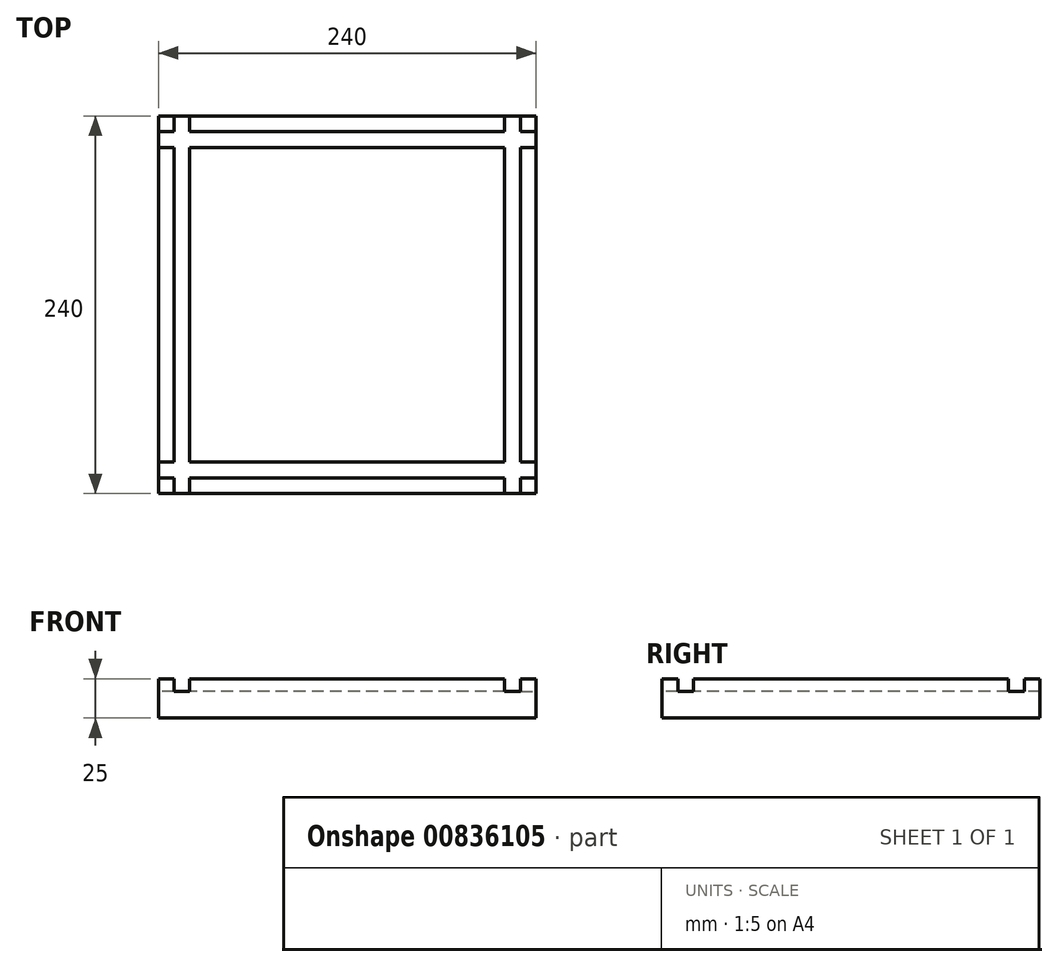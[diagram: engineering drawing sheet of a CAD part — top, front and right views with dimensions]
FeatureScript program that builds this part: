
annotation { "Feature Type Name" : "Feature", "Feature Type Description" : "" }
export const myFeature = defineFeature(function(context is Context, id is Id, definition is map)
    precondition{}
    {
        {
            var Q0;
            Q0=qCreatedBy(makeId("Top.planeOp"),FACE);
            var sketch = newSketch(context, id + "F0", { "sketchPlane" : qUnion([Q0])});
            skLineSegment(sketch, "E0.bottom", {"start": v(-120, 120) * mm, "end": v(120, 120) * mm});
            skLineSegment(sketch, "E0.top", {"start": v(-120, -120) * mm, "end": v(120, -120) * mm});
            skLineSegment(sketch, "E0.left", {"start": v(-120, 120) * mm, "end": v(-120, -120) * mm});
            skLineSegment(sketch, "E0.right", {"start": v(120, 120) * mm, "end": v(120, -120) * mm});
            skPoint(sketch, "E0.middle", {"position": v(0, 0) * mm});
            skSolve(sketch);
        }
        {
            var Q0;
            Q0 = qSketchRegion(id + "F0", true);
            extrude(context, id + "F1", {"entities" : qUnion([Q0]), "oppositeDirection" : true, "depth" : 25 * mm, "offsetDistance" : 25 * mm});
        }
        {
            var Q0;
            Q0=makeQuery(id+"F1.opExtrude","CAP_FACE",FACE,{"disambiguationData":[OSD([sQuery(id+"F0.wireOp",EDGE,"E0.bottom"),sQuery(id+"F0.wireOp",EDGE,"E0.top"),sQuery(id+"F0.wireOp",EDGE,"E0.left"),sQuery(id+"F0.wireOp",EDGE,"E0.right")])],"isStart":true});
            var sketch = newSketch(context, id + "F2", { "sketchPlane" : qUnion([Q0])});
            skLineSegment(sketch, "E1.bottom", {"start": v(-110, 120) * mm, "end": v(-100, 120) * mm});
            skLineSegment(sketch, "E1.top", {"start": v(-110, -120) * mm, "end": v(-100, -120) * mm});
            skLineSegment(sketch, "E1.left", {"start": v(-110, 120) * mm, "end": v(-110, -120) * mm});
            skLineSegment(sketch, "E1.right", {"start": v(-100, 120) * mm, "end": v(-100, -120) * mm});
            skLineSegment(sketch, "E2.bottom", {"start": v(-120, -100) * mm, "end": v(120, -100) * mm});
            skLineSegment(sketch, "E2.top", {"start": v(-120, -110) * mm, "end": v(120, -110) * mm});
            skLineSegment(sketch, "E2.left", {"start": v(-120, -100) * mm, "end": v(-120, -110) * mm});
            skLineSegment(sketch, "E2.right", {"start": v(120, -100) * mm, "end": v(120, -110) * mm});
            skLineSegment(sketch, "E3.bottom", {"start": v(110, -120) * mm, "end": v(100, -120) * mm});
            skLineSegment(sketch, "E3.top", {"start": v(110, 120) * mm, "end": v(100, 120) * mm});
            skLineSegment(sketch, "E3.left", {"start": v(110, -120) * mm, "end": v(110, 120) * mm});
            skLineSegment(sketch, "E3.right", {"start": v(100, -120) * mm, "end": v(100, 120) * mm});
            skLineSegment(sketch, "E4.bottom", {"start": v(120, 110) * mm, "end": v(-120, 110) * mm});
            skLineSegment(sketch, "E4.top", {"start": v(120, 100) * mm, "end": v(-120, 100) * mm});
            skLineSegment(sketch, "E4.left", {"start": v(120, 110) * mm, "end": v(120, 100) * mm});
            skLineSegment(sketch, "E4.right", {"start": v(-120, 110) * mm, "end": v(-120, 100) * mm});
            skSolve(sketch);
        }
        {
            var Q0;
            {var subQ0=sQuery(id+"F2.wireOp",EDGE,"E1.bottom");Q0=makeQuery(id+"F2.imprint","IMPRINT",FACE,{"disambiguationData":[TD([[makeQuery(id+"F2.imprint","IMPRINT",EDGE,{"derivedFrom":subQ0}),-1.0]])]});}
            var Q1;
            {var subQ0=sQuery(id+"F2.wireOp",EDGE,"E4.bottom");var subQ1=sQuery(id+"F2.wireOp",EDGE,"E1.left");var subQ2=makeQuery(id+"F2.imprint","INTERSECT",VERTEX,{"derivedFrom":[subQ1,subQ0]});Q1=makeQuery(id+"F2.imprint","IMPRINT",FACE,{"disambiguationData":[TD([[makeQuery(id+"F2.imprint","IMPRINT",EDGE,{"disambiguationData":[TD([[subQ2,-1.0]])],"derivedFrom":subQ1}),1.0]])]});}
            var Q2;
            {var subQ5=sQuery(id+"F2.wireOp",EDGE,"E4.right");Q2=makeQuery(id+"F2.imprint","IMPRINT",FACE,{"disambiguationData":[TD([[makeQuery(id+"F2.imprint","IMPRINT",EDGE,{"derivedFrom":subQ5}),1.0]])]});}
            var Q3;
            {var subQ0=sQuery(id+"F2.wireOp",EDGE,"E4.top");var subQ1=sQuery(id+"F2.wireOp",EDGE,"E1.left");var subQ2=makeQuery(id+"F2.imprint","INTERSECT",VERTEX,{"derivedFrom":[subQ1,subQ0]});Q3=makeQuery(id+"F2.imprint","IMPRINT",FACE,{"disambiguationData":[TD([[makeQuery(id+"F2.imprint","IMPRINT",EDGE,{"disambiguationData":[TD([[subQ2,-1.0]])],"derivedFrom":subQ1}),1.0]])]});}
            var Q4;
            {var subQ0=sQuery(id+"F2.wireOp",EDGE,"E4.bottom");var subQ1=sQuery(id+"F2.wireOp",EDGE,"E1.right");var subQ2=makeQuery(id+"F2.imprint","INTERSECT",VERTEX,{"derivedFrom":[subQ1,subQ0]});Q4=makeQuery(id+"F2.imprint","IMPRINT",FACE,{"disambiguationData":[TD([[makeQuery(id+"F2.imprint","IMPRINT",EDGE,{"disambiguationData":[TD([[subQ2,-1.0]])],"derivedFrom":subQ1}),1.0]])]});}
            var Q5;
            {var subQ0=sQuery(id+"F2.wireOp",EDGE,"E3.top");Q5=makeQuery(id+"F2.imprint","IMPRINT",FACE,{"disambiguationData":[TD([[makeQuery(id+"F2.imprint","IMPRINT",EDGE,{"derivedFrom":subQ0}),-1.0]])]});}
            var Q6;
            {var subQ5=sQuery(id+"F2.wireOp",EDGE,"E4.left");Q6=makeQuery(id+"F2.imprint","IMPRINT",FACE,{"disambiguationData":[TD([[makeQuery(id+"F2.imprint","IMPRINT",EDGE,{"derivedFrom":subQ5}),-1.0]])]});}
            var Q7;
            {var subQ0=sQuery(id+"F2.wireOp",EDGE,"E4.top");var subQ1=sQuery(id+"F2.wireOp",EDGE,"E3.left");var subQ2=makeQuery(id+"F2.imprint","INTERSECT",VERTEX,{"derivedFrom":[subQ1,subQ0]});Q7=makeQuery(id+"F2.imprint","IMPRINT",FACE,{"disambiguationData":[TD([[makeQuery(id+"F2.imprint","IMPRINT",EDGE,{"disambiguationData":[TD([[subQ2,-1.0]])],"derivedFrom":subQ1}),1.0]])]});}
            var Q8;
            {var subQ0=sQuery(id+"F2.wireOp",EDGE,"E3.right");var subQ1=sQuery(id+"F2.wireOp",EDGE,"E2.bottom");var subQ2=makeQuery(id+"F2.imprint","INTERSECT",VERTEX,{"derivedFrom":[subQ1,subQ0]});Q8=makeQuery(id+"F2.imprint","IMPRINT",FACE,{"disambiguationData":[TD([[makeQuery(id+"F2.imprint","IMPRINT",EDGE,{"disambiguationData":[TD([[subQ2,-1.0]])],"derivedFrom":subQ1}),1.0]])]});}
            var Q9;
            {var subQ5=sQuery(id+"F2.wireOp",EDGE,"E3.bottom");Q9=makeQuery(id+"F2.imprint","IMPRINT",FACE,{"disambiguationData":[TD([[makeQuery(id+"F2.imprint","IMPRINT",EDGE,{"derivedFrom":subQ5}),1.0]])]});}
            var Q10;
            {var subQ0=sQuery(id+"F2.wireOp",EDGE,"E3.right");var subQ1=sQuery(id+"F2.wireOp",EDGE,"E2.bottom");var subQ2=makeQuery(id+"F2.imprint","INTERSECT",VERTEX,{"derivedFrom":[subQ1,subQ0]});Q10=makeQuery(id+"F2.imprint","IMPRINT",FACE,{"disambiguationData":[TD([[makeQuery(id+"F2.imprint","IMPRINT",EDGE,{"disambiguationData":[TD([[subQ2,-1.0]])],"derivedFrom":subQ1}),-1.0]])]});}
            var Q11;
            {var subQ0=sQuery(id+"F2.wireOp",EDGE,"E2.right");Q11=makeQuery(id+"F2.imprint","IMPRINT",FACE,{"disambiguationData":[TD([[makeQuery(id+"F2.imprint","IMPRINT",EDGE,{"derivedFrom":subQ0}),-1.0]])]});}
            var Q12;
            {var subQ0=sQuery(id+"F2.wireOp",EDGE,"E2.bottom");var subQ1=sQuery(id+"F2.wireOp",EDGE,"E1.right");var subQ2=makeQuery(id+"F2.imprint","INTERSECT",VERTEX,{"derivedFrom":[subQ1,subQ0]});Q12=makeQuery(id+"F2.imprint","IMPRINT",FACE,{"disambiguationData":[TD([[makeQuery(id+"F2.imprint","IMPRINT",EDGE,{"disambiguationData":[TD([[subQ2,-1.0]])],"derivedFrom":subQ1}),1.0]])]});}
            var Q13;
            {var subQ0=sQuery(id+"F2.wireOp",EDGE,"E2.bottom");var subQ1=sQuery(id+"F2.wireOp",EDGE,"E1.left");var subQ2=makeQuery(id+"F2.imprint","INTERSECT",VERTEX,{"derivedFrom":[subQ1,subQ0]});Q13=makeQuery(id+"F2.imprint","IMPRINT",FACE,{"disambiguationData":[TD([[makeQuery(id+"F2.imprint","IMPRINT",EDGE,{"disambiguationData":[TD([[subQ2,-1.0]])],"derivedFrom":subQ1}),1.0]])]});}
            var Q14;
            {var subQ0=sQuery(id+"F2.wireOp",EDGE,"E1.top");Q14=makeQuery(id+"F2.imprint","IMPRINT",FACE,{"disambiguationData":[TD([[makeQuery(id+"F2.imprint","IMPRINT",EDGE,{"derivedFrom":subQ0}),1.0]])]});}
            var Q15;
            {var subQ5=sQuery(id+"F2.wireOp",EDGE,"E2.left");Q15=makeQuery(id+"F2.imprint","IMPRINT",FACE,{"disambiguationData":[TD([[makeQuery(id+"F2.imprint","IMPRINT",EDGE,{"derivedFrom":subQ5}),1.0]])]});}
            extrude(context, id + "F3", {"entities" : qUnion([Q0, Q1, Q2, Q3, Q4, Q5, Q6, Q7, Q8, Q9, Q10, Q11, Q12, Q13, Q14, Q15]), "operationType" : NewBodyOperationType.REMOVE, "oppositeDirection" : true, "depth" : 8 * mm, "offsetDistance" : 25 * mm});
        }
    });
